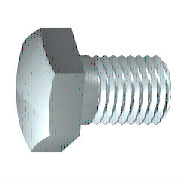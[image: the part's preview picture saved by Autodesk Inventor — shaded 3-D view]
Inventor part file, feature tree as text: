
AUTODESK INVENTOR PART (.ipt)
format: ipt  version: 2023.2 (Build 272271030, 271C)  size: 192,000 bytes
history: native  units: mm (DEFAULTED — no unit token found)
features: sketch x3, extrude x1, chamfer x1, plane x1
ambient origin geometry x7: Origin, YZ Plane, XZ Plane, X Axis, Y Axis, Z Axis, Center Point
bodies: Solid1 (feature_tree), Body (feature_tree)
feature tree (6):
  extrude  "Head"  Depth=44.7mm
  chamfer  "Chamfer1"  Distance=6.9mm
  plane  "Work Plane1"
  sketch  "Sketch1"  dims[d0=50.0mm d1=44.7mm]
  sketch  "Sketch2"  dims[d2=12.0mm]
  sketch  "Sketch4"  dims[d12=90.0deg d3=6.9mm d4=0.0mm d5=30.0deg d21=90.0deg d6=1.073538mm d7=1.073638mm d8=0.0mm d9=0.6001mm d10=16.63mm d11=18.0mm d13=1.073638mm d14=12.0mm d15=44.7mm d16=0.0mm d19=18.0mm d55=45.0deg d57=0.0mm d58=0.0mm]
